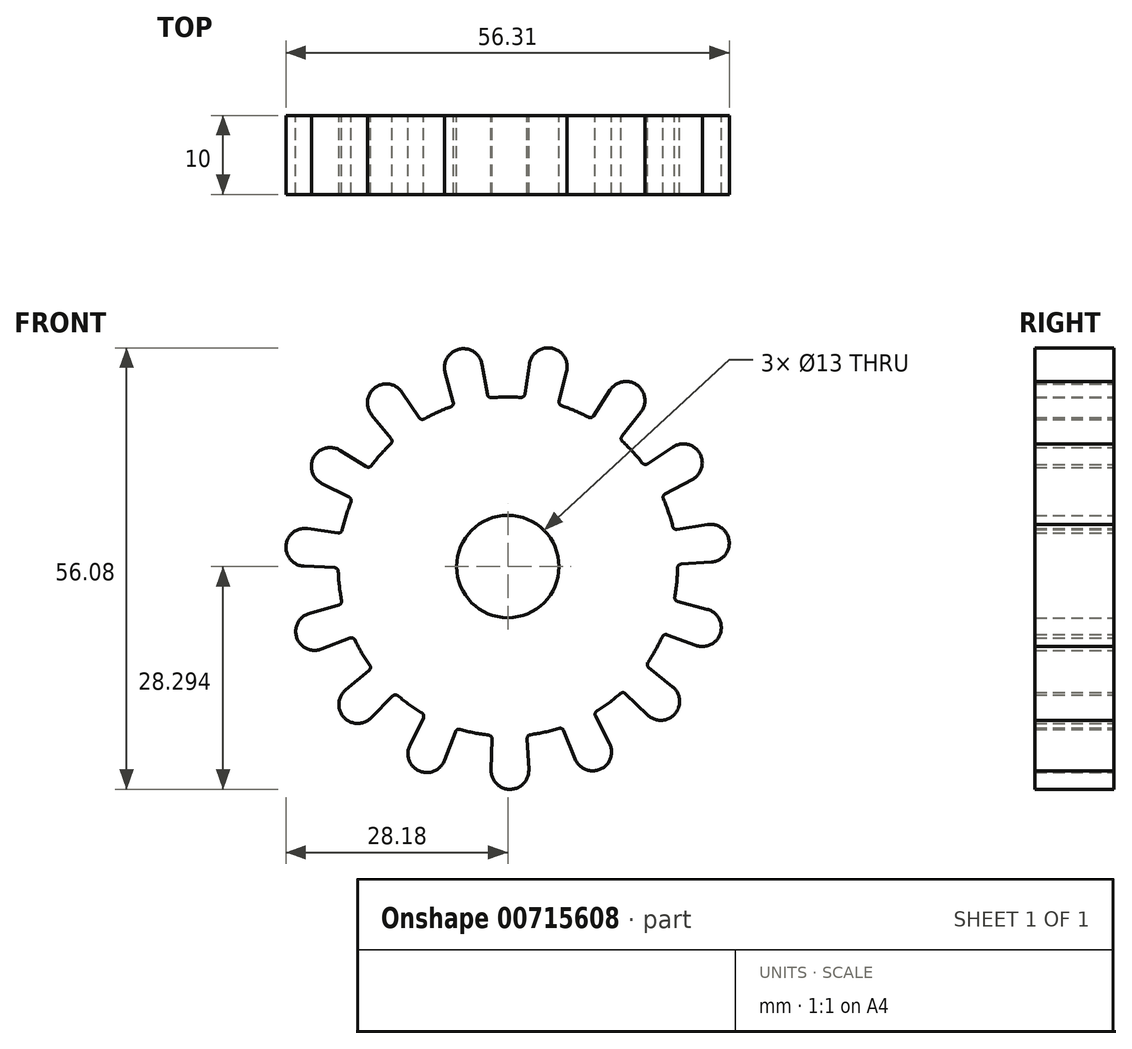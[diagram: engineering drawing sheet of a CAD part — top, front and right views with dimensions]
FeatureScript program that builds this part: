
annotation { "Feature Type Name" : "Feature", "Feature Type Description" : "" }
export const myFeature = defineFeature(function(context is Context, id is Id, definition is map)
    precondition{}
    {
        {
            var Q0;
            Q0=qCreatedBy(makeId("Front.planeOp"),FACE);
            var sketch = newSketch(context, id + "F0", { "sketchPlane" : qUnion([Q0])});
            skCircle(sketch, "E0", {"center": v(-0.06, 0.27) * mm, "radius": 6.5 * mm});
            skCircle(sketch, "E1", {"center": v(-0.06, 0.27) * mm, "radius": 25.9 * mm, "construction": true});
            skCircle(sketch, "E2", {"center": v(-0.06, 0.27) * mm, "radius": 21.55 * mm});
            skCircle(sketch, "E3", {"center": v(14.95, 21.38) * mm, "radius": 2.4 * mm});
            skLineSegment(sketch, "E4", {"start": v(12.93, 22.68) * mm, "end": v(10.83, 19.41) * mm});
            skLineSegment(sketch, "E5", {"start": v(16.84, 19.9) * mm, "end": v(14.44, 16.84) * mm});
            skArc(sketch, "E6", {"start": v(14.44, 16.84) * mm, "mid": v(14.34, 16.5) * mm, "end": v(14.5, 16.16) * mm});
            skArc(sketch, "E7", {"start": v(10.17, 19.24) * mm, "mid": v(10.53, 19.2) * mm, "end": v(10.83, 19.41) * mm});
            skCircle(sketch, "E8.1.0", {"center": v(5.07, 25.66) * mm, "radius": 2.4 * mm});
            skLineSegment(sketch, "E8.1.1", {"start": v(2.7, 26.03) * mm, "end": v(2.1, 22.19) * mm});
            skArc(sketch, "E8.1.2", {"start": v(1.57, 21.76) * mm, "mid": v(1.92, 21.87) * mm, "end": v(2.1, 22.19) * mm});
            skArc(sketch, "E8.1.3", {"start": v(6.45, 21.3) * mm, "mid": v(6.5, 20.95) * mm, "end": v(6.78, 20.71) * mm});
            skLineSegment(sketch, "E8.1.4", {"start": v(7.4, 25.08) * mm, "end": v(6.45, 21.3) * mm});
            skCircle(sketch, "E9.1.2.0", {"center": v(-5.7, 25.55) * mm, "radius": 2.4 * mm});
            skLineSegment(sketch, "E9.2.2.0", {"start": v(-8.02, 24.92) * mm, "end": v(-7, 21.17) * mm});
            skArc(sketch, "E9.5.2.0", {"start": v(-7.31, 20.57) * mm, "mid": v(-7.04, 20.8) * mm, "end": v(-7, 21.17) * mm});
            skArc(sketch, "E9.9.2.0", {"start": v(-2.67, 22.14) * mm, "mid": v(-2.48, 21.82) * mm, "end": v(-2.13, 21.72) * mm});
            skLineSegment(sketch, "E9.13.2.0", {"start": v(-3.34, 25.97) * mm, "end": v(-2.67, 22.14) * mm});
            skCircle(sketch, "E9.1.3.0", {"center": v(-15.5, 21.07) * mm, "radius": 2.4 * mm});
            skLineSegment(sketch, "E9.2.3.0", {"start": v(-17.36, 19.55) * mm, "end": v(-14.9, 16.54) * mm});
            skArc(sketch, "E9.5.3.0", {"start": v(-14.94, 15.86) * mm, "mid": v(-14.78, 16.2) * mm, "end": v(-14.9, 16.54) * mm});
            skArc(sketch, "E9.9.3.0", {"start": v(-11.34, 19.19) * mm, "mid": v(-11.04, 18.98) * mm, "end": v(-10.67, 19.03) * mm});
            skLineSegment(sketch, "E9.13.3.0", {"start": v(-13.5, 22.41) * mm, "end": v(-11.34, 19.19) * mm});
            skCircle(sketch, "E9.1.4.0", {"center": v(-22.62, 13) * mm, "radius": 2.4 * mm});
            skLineSegment(sketch, "E9.2.4.0", {"start": v(-23.7, 10.85) * mm, "end": v(-20.23, 9.1) * mm});
            skArc(sketch, "E9.5.4.0", {"start": v(-20, 8.46) * mm, "mid": v(-19.99, 8.83) * mm, "end": v(-20.23, 9.1) * mm});
            skArc(sketch, "E9.9.4.0", {"start": v(-18.05, 12.96) * mm, "mid": v(-17.7, 12.9) * mm, "end": v(-17.38, 13.1) * mm});
            skLineSegment(sketch, "E9.13.4.0", {"start": v(-21.35, 15.03) * mm, "end": v(-18.05, 12.96) * mm});
            skCircle(sketch, "E9.1.5.0", {"center": v(-25.84, 2.72) * mm, "radius": 2.4 * mm});
            skLineSegment(sketch, "E9.2.5.0", {"start": v(-25.96, 0.32) * mm, "end": v(-22.08, 0.13) * mm});
            skArc(sketch, "E9.5.5.0", {"start": v(-21.6, -0.35) * mm, "mid": v(-21.74, -0.02) * mm, "end": v(-22.08, 0.13) * mm});
            skArc(sketch, "E9.9.5.0", {"start": v(-21.66, 4.55) * mm, "mid": v(-21.3, 4.63) * mm, "end": v(-21.1, 4.94) * mm});
            skLineSegment(sketch, "E9.13.5.0", {"start": v(-25.5, 5.1) * mm, "end": v(-21.66, 4.55) * mm});
            skCircle(sketch, "E9.1.6.0", {"center": v(-24.6, -7.98) * mm, "radius": 2.4 * mm});
            skLineSegment(sketch, "E9.2.6.0", {"start": v(-23.74, -10.22) * mm, "end": v(-20.12, -8.8) * mm});
            skArc(sketch, "E9.5.6.0", {"start": v(-19.48, -9.06) * mm, "mid": v(-19.75, -8.8) * mm, "end": v(-20.12, -8.8) * mm});
            skArc(sketch, "E9.9.6.0", {"start": v(-21.53, -4.6) * mm, "mid": v(-21.24, -4.38) * mm, "end": v(-21.18, -4.02) * mm});
            skLineSegment(sketch, "E9.13.6.0", {"start": v(-25.27, -5.67) * mm, "end": v(-21.53, -4.6) * mm});
            skCircle(sketch, "E9.1.7.0", {"center": v(-19.13, -17.25) * mm, "radius": 2.4 * mm});
            skLineSegment(sketch, "E9.2.7.0", {"start": v(-17.42, -18.94) * mm, "end": v(-14.69, -16.18) * mm});
            skArc(sketch, "E9.5.7.0", {"start": v(-14, -16.15) * mm, "mid": v(-14.35, -16.03) * mm, "end": v(-14.69, -16.18) * mm});
            skArc(sketch, "E9.9.7.0", {"start": v(-17.69, -12.92) * mm, "mid": v(-17.51, -12.6) * mm, "end": v(-17.6, -12.24) * mm});
            skLineSegment(sketch, "E9.13.7.0", {"start": v(-20.67, -15.41) * mm, "end": v(-17.69, -12.92) * mm});
            skCircle(sketch, "E9.1.8.0", {"center": v(-10.35, -23.5) * mm, "radius": 2.4 * mm});
            skLineSegment(sketch, "E9.2.8.0", {"start": v(-8.1, -24.34) * mm, "end": v(-6.73, -20.7) * mm});
            skArc(sketch, "E9.5.8.0", {"start": v(-6.12, -20.4) * mm, "mid": v(-6.48, -20.44) * mm, "end": v(-6.73, -20.7) * mm});
            skArc(sketch, "E9.9.8.0", {"start": v(-10.8, -18.95) * mm, "mid": v(-10.77, -18.58) * mm, "end": v(-11, -18.3) * mm});
            skLineSegment(sketch, "E9.13.8.0", {"start": v(-12.5, -22.44) * mm, "end": v(-10.8, -18.95) * mm});
            skCircle(sketch, "E9.1.9.0", {"center": v(0.2, -25.62) * mm, "radius": 2.4 * mm});
            skLineSegment(sketch, "E9.2.9.0", {"start": v(2.6, -25.49) * mm, "end": v(2.38, -21.6) * mm});
            skArc(sketch, "E9.5.9.0", {"start": v(2.81, -21.08) * mm, "mid": v(2.5, -21.26) * mm, "end": v(2.38, -21.6) * mm});
            skArc(sketch, "E9.9.9.0", {"start": v(-2.05, -21.65) * mm, "mid": v(-2.17, -21.3) * mm, "end": v(-2.5, -21.14) * mm});
            skLineSegment(sketch, "E9.13.9.0", {"start": v(-2.2, -25.54) * mm, "end": v(-2.05, -21.65) * mm});
            skCircle(sketch, "E9.1.10.0", {"center": v(10.72, -23.28) * mm, "radius": 2.4 * mm});
            skLineSegment(sketch, "E9.2.10.0", {"start": v(12.85, -22.18) * mm, "end": v(11.07, -18.72) * mm});
            skArc(sketch, "E9.5.10.0", {"start": v(11.25, -18.07) * mm, "mid": v(11.03, -18.36) * mm, "end": v(11.07, -18.72) * mm});
            skArc(sketch, "E9.9.10.0", {"start": v(7.04, -20.57) * mm, "mid": v(6.79, -20.3) * mm, "end": v(6.42, -20.28) * mm});
            skLineSegment(sketch, "E9.13.10.0", {"start": v(8.49, -24.17) * mm, "end": v(7.04, -20.57) * mm});
            skCircle(sketch, "E9.1.11.0", {"center": v(19.36, -16.86) * mm, "radius": 2.4 * mm});
            skLineSegment(sketch, "E9.2.11.0", {"start": v(20.87, -14.99) * mm, "end": v(17.83, -12.55) * mm});
            skArc(sketch, "E9.5.11.0", {"start": v(17.73, -11.88) * mm, "mid": v(17.65, -12.24) * mm, "end": v(17.83, -12.55) * mm});
            skArc(sketch, "E9.9.11.0", {"start": v(14.9, -15.88) * mm, "mid": v(14.56, -15.74) * mm, "end": v(14.22, -15.86) * mm});
            skLineSegment(sketch, "E9.13.11.0", {"start": v(17.7, -18.58) * mm, "end": v(14.9, -15.88) * mm});
            skCircle(sketch, "E9.1.12.0", {"center": v(24.65, -7.48) * mm, "radius": 2.4 * mm});
            skLineSegment(sketch, "E9.2.12.0", {"start": v(25.26, -5.16) * mm, "end": v(21.5, -4.17) * mm});
            skArc(sketch, "E9.5.12.0", {"start": v(21.14, -3.6) * mm, "mid": v(21.21, -3.95) * mm, "end": v(21.5, -4.17) * mm});
            skArc(sketch, "E9.9.12.0", {"start": v(20.18, -8.4) * mm, "mid": v(19.81, -8.4) * mm, "end": v(19.55, -8.66) * mm});
            skLineSegment(sketch, "E9.13.12.0", {"start": v(23.83, -9.73) * mm, "end": v(20.18, -8.4) * mm});
            skCircle(sketch, "E9.1.13.0", {"center": v(25.67, 3.24) * mm, "radius": 2.4 * mm});
            skLineSegment(sketch, "E9.2.13.0", {"start": v(25.28, 5.61) * mm, "end": v(21.45, 4.99) * mm});
            skArc(sketch, "E9.5.13.0", {"start": v(20.88, 5.36) * mm, "mid": v(21.09, 5.07) * mm, "end": v(21.45, 4.99) * mm});
            skArc(sketch, "E9.9.13.0", {"start": v(21.96, 0.58) * mm, "mid": v(21.63, 0.43) * mm, "end": v(21.49, 0.09) * mm});
            skLineSegment(sketch, "E9.13.13.0", {"start": v(25.83, 0.85) * mm, "end": v(21.96, 0.58) * mm});
            skCircle(sketch, "E9.1.14.0", {"center": v(22.24, 13.45) * mm, "radius": 2.4 * mm});
            skLineSegment(sketch, "E9.2.14.0", {"start": v(20.92, 15.46) * mm, "end": v(17.67, 13.33) * mm});
            skArc(sketch, "E9.5.14.0", {"start": v(17, 13.44) * mm, "mid": v(17.31, 13.25) * mm, "end": v(17.67, 13.33) * mm});
            skArc(sketch, "E9.9.14.0", {"start": v(19.93, 9.51) * mm, "mid": v(19.69, 9.23) * mm, "end": v(19.7, 8.87) * mm});
            skLineSegment(sketch, "E9.13.14.0", {"start": v(23.36, 11.33) * mm, "end": v(19.93, 9.51) * mm});
            skSolve(sketch);
        }
        {
            var Q0;
            Q0 = qSketchRegion(id + "F0", true);
            extrude(context, id + "F1", {"entities" : qUnion([Q0]), "depth" : 10 * mm, "offsetDistance" : 25 * mm});
        }
    });
